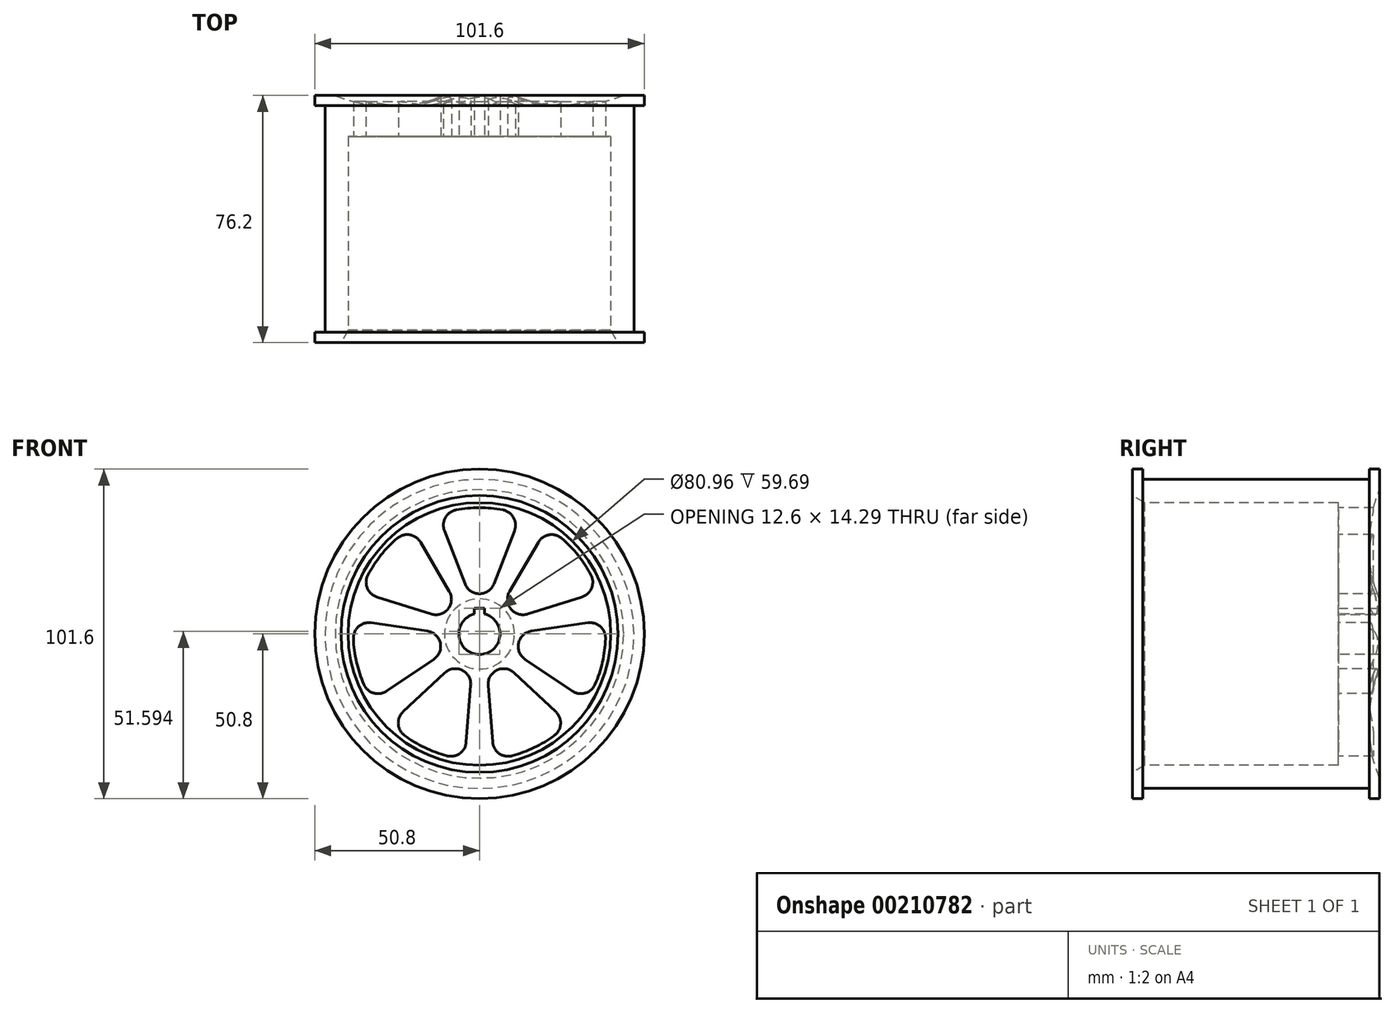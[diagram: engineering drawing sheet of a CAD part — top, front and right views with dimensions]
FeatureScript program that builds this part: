
annotation { "Feature Type Name" : "Feature", "Feature Type Description" : "" }
export const myFeature = defineFeature(function(context is Context, id is Id, definition is map)
    precondition{}
    {
        {
            var Q0;
            Q0=qCreatedBy(makeId("Right.planeOp"),FACE);
            var sketch = newSketch(context, id + "F0", { "sketchPlane" : qUnion([Q0])});
            skLineSegment(sketch, "E0.bottom", {"start": v(-38.1, 40.48) * mm, "end": v(25.4, 40.48) * mm});
            skLineSegment(sketch, "E0.top", {"start": v(-38.1, 50.8) * mm, "end": v(38.1, 50.8) * mm, "construction": true});
            skLineSegment(sketch, "E0.left", {"start": v(-38.1, 40.48) * mm, "end": v(-38.1, 50.8) * mm});
            skLineSegment(sketch, "E1", {"start": v(-75.27, 0) * mm, "end": v(76.28, 0) * mm, "construction": true});
            skLineSegment(sketch, "E2", {"start": v(-34.93, 50.8) * mm, "end": v(-34.93, 47.62) * mm});
            skLineSegment(sketch, "E3", {"start": v(-34.93, 47.62) * mm, "end": v(34.93, 47.62) * mm});
            skLineSegment(sketch, "E4", {"start": v(34.93, 47.62) * mm, "end": v(34.93, 50.8) * mm});
            skLineSegment(sketch, "E5", {"start": v(34.93, 50.8) * mm, "end": v(38.1, 50.8) * mm});
            skLineSegment(sketch, "E6", {"start": v(-38.1, 50.8) * mm, "end": v(-34.93, 50.8) * mm});
            skLineSegment(sketch, "E7", {"start": v(25.4, 40.48) * mm, "end": v(25.4, 6.35) * mm});
            skLineSegment(sketch, "E8", {"start": v(25.4, 6.35) * mm, "end": v(38.1, 6.35) * mm});
            skLineSegment(sketch, "E9", {"start": v(38.1, 50.8) * mm, "end": v(38.1, 6.35) * mm});
            skSolve(sketch);
        }
        {
            var Q0;
            Q0 = qSketchRegion(id + "F0", true);
            var Q1;
            Q1=sQuery(id+"F0.wireOp",EDGE,"E1");
            revolve(context, id + "F1", {"entities" : qUnion([Q0]), "axis" : qUnion([Q1]), "revolveType" : RevolveType.FULL});
        }
        {
            var Q0;
            Q0=makeQuery(id+"F1.opRevolve","SWEPT_FACE",FACE,{"disambiguationData":[OSD([sQuery(id+"F0.wireOp",EDGE,"E9")])]});
            var sketch = newSketch(context, id + "F2", { "sketchPlane" : qUnion([Q0])});
            skLineSegment(sketch, "E10.bottom", {"start": v(-1.59, 7.94) * mm, "end": v(1.59, 7.94) * mm});
            skLineSegment(sketch, "E10.top", {"start": v(-1.59, 4.76) * mm, "end": v(1.59, 4.76) * mm});
            skLineSegment(sketch, "E10.left", {"start": v(-1.59, 7.94) * mm, "end": v(-1.59, 4.76) * mm});
            skLineSegment(sketch, "E10.right", {"start": v(1.59, 7.94) * mm, "end": v(1.59, 4.76) * mm});
            skLineSegment(sketch, "E11", {"start": v(-1.59, 7.94) * mm, "end": v(1.59, 4.76) * mm, "construction": true});
            skPoint(sketch, "E12", {"position": v(0, 6.35) * mm});
            skSolve(sketch);
        }
        {
            var Q0;
            Q0 = qSketchRegion(id + "F2", true);
            extrude(context, id + "F3", {"entities" : qUnion([Q0]), "operationType" : NewBodyOperationType.REMOVE, "endBound" : BoundingType.UP_TO_NEXT, "oppositeDirection" : true, "depth" : 25.4 * mm});
        }
        {
            var Q0;
            Q0=qCreatedBy(makeId("Right.planeOp"),FACE);
            var sketch = newSketch(context, id + "F4", { "sketchPlane" : qUnion([Q0])});
            skLineSegment(sketch, "E13", {"start": v(-46.97, 0) * mm, "end": v(51.22, 0) * mm, "construction": true});
            skLineSegment(sketch, "E14.0", {"start": v(38.1, 0) * mm, "end": v(38.1, 50.8) * mm, "construction": true});
            skPoint(sketch, "E15.orphan", {"position": v(38.1, -50.8) * mm});
            skPoint(sketch, "E16", {"position": v(38.1, 44.45) * mm});
            skPoint(sketch, "E17", {"position": v(38.1, 10.8) * mm});
            skArc(sketch, "E18", {"start": v(38.1, 44.45) * mm, "mid": v(34.8, 27.62) * mm, "end": v(38.1, 10.8) * mm});
            skLineSegment(sketch, "E19", {"start": v(38.1, 44.45) * mm, "end": v(38.1, 10.8) * mm});
            skSolve(sketch);
        }
        {
            var Q0;
            Q0 = qSketchRegion(id + "F4", true);
            var Q1;
            Q1=sQuery(id+"F4.wireOp",EDGE,"E13");
            revolve(context, id + "F5", {"operationType" : NewBodyOperationType.REMOVE, "entities" : qUnion([Q0]), "axis" : qUnion([Q1]), "revolveType" : RevolveType.FULL, "oppositeDirection" : true});
        }
        {
            var Q0;
            Q0=makeQuery(id+"F1.opRevolve","SWEPT_FACE",FACE,{"disambiguationData":[OSD([sQuery(id+"F0.wireOp",EDGE,"E7")])]});
            var sketch = newSketch(context, id + "F6", { "sketchPlane" : qUnion([Q0])});
            skCircle(sketch, "E20.0", {"center": v(0, 0) * mm, "radius": 10.8 * mm, "construction": true});
            skCircle(sketch, "E21.0", {"center": v(0, 0) * mm, "radius": 40.48 * mm, "construction": true});
            skCircle(sketch, "E22", {"center": v(0, 0) * mm, "radius": 12.38 * mm, "construction": true});
            skArc(sketch, "E23", {"start": v(7.24, 38.21) * mm, "mid": v(0, 38.9) * mm, "end": v(-7.24, 38.21) * mm});
            skLineSegment(sketch, "E24", {"start": v(0, 0) * mm, "end": v(0, 54.52) * mm, "construction": true});
            skLineSegment(sketch, "E25", {"start": v(-6.35, 33.54) * mm, "end": v(6.35, 33.54) * mm, "construction": true});
            skPoint(sketch, "E26", {"position": v(0, 33.54) * mm});
            skArc(sketch, "E27", {"start": v(10.8, 31.81) * mm, "mid": v(10.51, 35.85) * mm, "end": v(7.24, 38.21) * mm});
            skArc(sketch, "E28", {"start": v(-7.24, 38.21) * mm, "mid": v(-10.51, 35.85) * mm, "end": v(-10.8, 31.81) * mm});
            skArc(sketch, "E29", {"start": v(-4.44, 15.42) * mm, "mid": v(0, 12.38) * mm, "end": v(4.44, 15.42) * mm});
            skLineSegment(sketch, "E30", {"start": v(-10.8, 31.81) * mm, "end": v(-4.44, 15.42) * mm});
            skLineSegment(sketch, "E31", {"start": v(4.44, 15.42) * mm, "end": v(10.8, 31.81) * mm});
            skArc(sketch, "E32.1.0", {"start": v(-14.83, 6.15) * mm, "mid": v(-9.68, 7.72) * mm, "end": v(-9.3, 13.09) * mm});
            skLineSegment(sketch, "E32.1.1", {"start": v(-9.3, 13.09) * mm, "end": v(-18.15, 28.27) * mm});
            skLineSegment(sketch, "E32.1.2", {"start": v(-31.6, 11.4) * mm, "end": v(-14.83, 6.15) * mm});
            skArc(sketch, "E32.1.3", {"start": v(-34.39, 18.17) * mm, "mid": v(-34.58, 14.13) * mm, "end": v(-31.6, 11.4) * mm});
            skArc(sketch, "E32.1.4", {"start": v(-25.37, 29.48) * mm, "mid": v(-30.4, 24.25) * mm, "end": v(-34.39, 18.17) * mm});
            skArc(sketch, "E32.1.5", {"start": v(-18.15, 28.27) * mm, "mid": v(-21.47, 30.57) * mm, "end": v(-25.37, 29.48) * mm});
            skArc(sketch, "E32.2.0", {"start": v(-14.05, -7.76) * mm, "mid": v(-12.07, -2.76) * mm, "end": v(-16.03, 0.9) * mm});
            skLineSegment(sketch, "E32.2.1", {"start": v(-16.03, 0.9) * mm, "end": v(-33.42, 3.44) * mm});
            skLineSegment(sketch, "E32.2.2", {"start": v(-28.62, -17.6) * mm, "end": v(-14.05, -7.76) * mm});
            skArc(sketch, "E32.2.3", {"start": v(-35.65, -15.56) * mm, "mid": v(-32.6, -18.23) * mm, "end": v(-28.62, -17.6) * mm});
            skArc(sketch, "E32.2.4", {"start": v(-38.87, -1.45) * mm, "mid": v(-37.92, -8.65) * mm, "end": v(-35.65, -15.56) * mm});
            skArc(sketch, "E32.2.5", {"start": v(-33.42, 3.44) * mm, "mid": v(-37.29, 2.27) * mm, "end": v(-38.87, -1.45) * mm});
            skArc(sketch, "E32.3.0", {"start": v(-2.7, -15.82) * mm, "mid": v(-5.37, -11.16) * mm, "end": v(-10.7, -11.97) * mm});
            skLineSegment(sketch, "E32.3.1", {"start": v(-10.7, -11.97) * mm, "end": v(-23.53, -23.98) * mm});
            skLineSegment(sketch, "E32.3.2", {"start": v(-4.08, -33.35) * mm, "end": v(-2.7, -15.82) * mm});
            skArc(sketch, "E32.3.3", {"start": v(-10.06, -37.57) * mm, "mid": v(-6.08, -36.86) * mm, "end": v(-4.08, -33.35) * mm});
            skArc(sketch, "E32.3.4", {"start": v(-23.1, -31.3) * mm, "mid": v(-16.88, -35.04) * mm, "end": v(-10.06, -37.57) * mm});
            skArc(sketch, "E32.3.5", {"start": v(-23.53, -23.98) * mm, "mid": v(-25.03, -27.74) * mm, "end": v(-23.1, -31.3) * mm});
            skArc(sketch, "E32.4.0", {"start": v(10.7, -11.97) * mm, "mid": v(5.37, -11.16) * mm, "end": v(2.7, -15.82) * mm});
            skLineSegment(sketch, "E32.4.1", {"start": v(2.7, -15.82) * mm, "end": v(4.08, -33.35) * mm});
            skLineSegment(sketch, "E32.4.2", {"start": v(23.53, -23.98) * mm, "end": v(10.7, -11.97) * mm});
            skArc(sketch, "E32.4.3", {"start": v(23.1, -31.3) * mm, "mid": v(25.03, -27.74) * mm, "end": v(23.53, -23.98) * mm});
            skArc(sketch, "E32.4.4", {"start": v(10.06, -37.57) * mm, "mid": v(16.88, -35.04) * mm, "end": v(23.1, -31.3) * mm});
            skArc(sketch, "E32.4.5", {"start": v(4.08, -33.35) * mm, "mid": v(6.08, -36.86) * mm, "end": v(10.06, -37.57) * mm});
            skArc(sketch, "E32.5.0", {"start": v(16.03, 0.9) * mm, "mid": v(12.07, -2.76) * mm, "end": v(14.05, -7.76) * mm});
            skLineSegment(sketch, "E32.5.1", {"start": v(14.05, -7.76) * mm, "end": v(28.62, -17.6) * mm});
            skLineSegment(sketch, "E32.5.2", {"start": v(33.42, 3.44) * mm, "end": v(16.03, 0.9) * mm});
            skArc(sketch, "E32.5.3", {"start": v(38.87, -1.45) * mm, "mid": v(37.29, 2.27) * mm, "end": v(33.42, 3.44) * mm});
            skArc(sketch, "E32.5.4", {"start": v(35.65, -15.56) * mm, "mid": v(37.92, -8.65) * mm, "end": v(38.87, -1.45) * mm});
            skArc(sketch, "E32.5.5", {"start": v(28.62, -17.6) * mm, "mid": v(32.6, -18.23) * mm, "end": v(35.65, -15.56) * mm});
            skArc(sketch, "E32.6.0", {"start": v(9.3, 13.09) * mm, "mid": v(9.68, 7.72) * mm, "end": v(14.83, 6.15) * mm});
            skLineSegment(sketch, "E32.6.1", {"start": v(14.83, 6.15) * mm, "end": v(31.6, 11.4) * mm});
            skLineSegment(sketch, "E32.6.2", {"start": v(18.15, 28.27) * mm, "end": v(9.3, 13.09) * mm});
            skArc(sketch, "E32.6.3", {"start": v(25.37, 29.48) * mm, "mid": v(21.47, 30.57) * mm, "end": v(18.15, 28.27) * mm});
            skArc(sketch, "E32.6.4", {"start": v(34.39, 18.17) * mm, "mid": v(30.4, 24.25) * mm, "end": v(25.37, 29.48) * mm});
            skArc(sketch, "E32.6.5", {"start": v(31.6, 11.4) * mm, "mid": v(34.58, 14.13) * mm, "end": v(34.39, 18.17) * mm});
            skSolve(sketch);
        }
        {
            var Q0;
            Q0 = qSketchRegion(id + "F6", true);
            extrude(context, id + "F7", {"entities" : qUnion([Q0]), "operationType" : NewBodyOperationType.REMOVE, "endBound" : BoundingType.UP_TO_NEXT, "oppositeDirection" : true, "depth" : 25.4 * mm});
        }
        {
            var Q0;
            Q0=makeQuery(id+"F1.opRevolve","SWEPT_EDGE",EDGE,{"disambiguationData":[OSD([sQuery(id+"F0.wireOp",EDGE,"E0.bottom"),sQuery(id+"F0.wireOp",EDGE,"E0.left")])]});
            chamfer(context, id + "F8", {"entities" : qUnion([Q0]), "chamferType" : ChamferType.OFFSET_ANGLE, "width" : 3.8 * mm, "oppositeDirection" : false, "angle" : 30 * degree, "tangentPropagation" : true});
        }
    });
